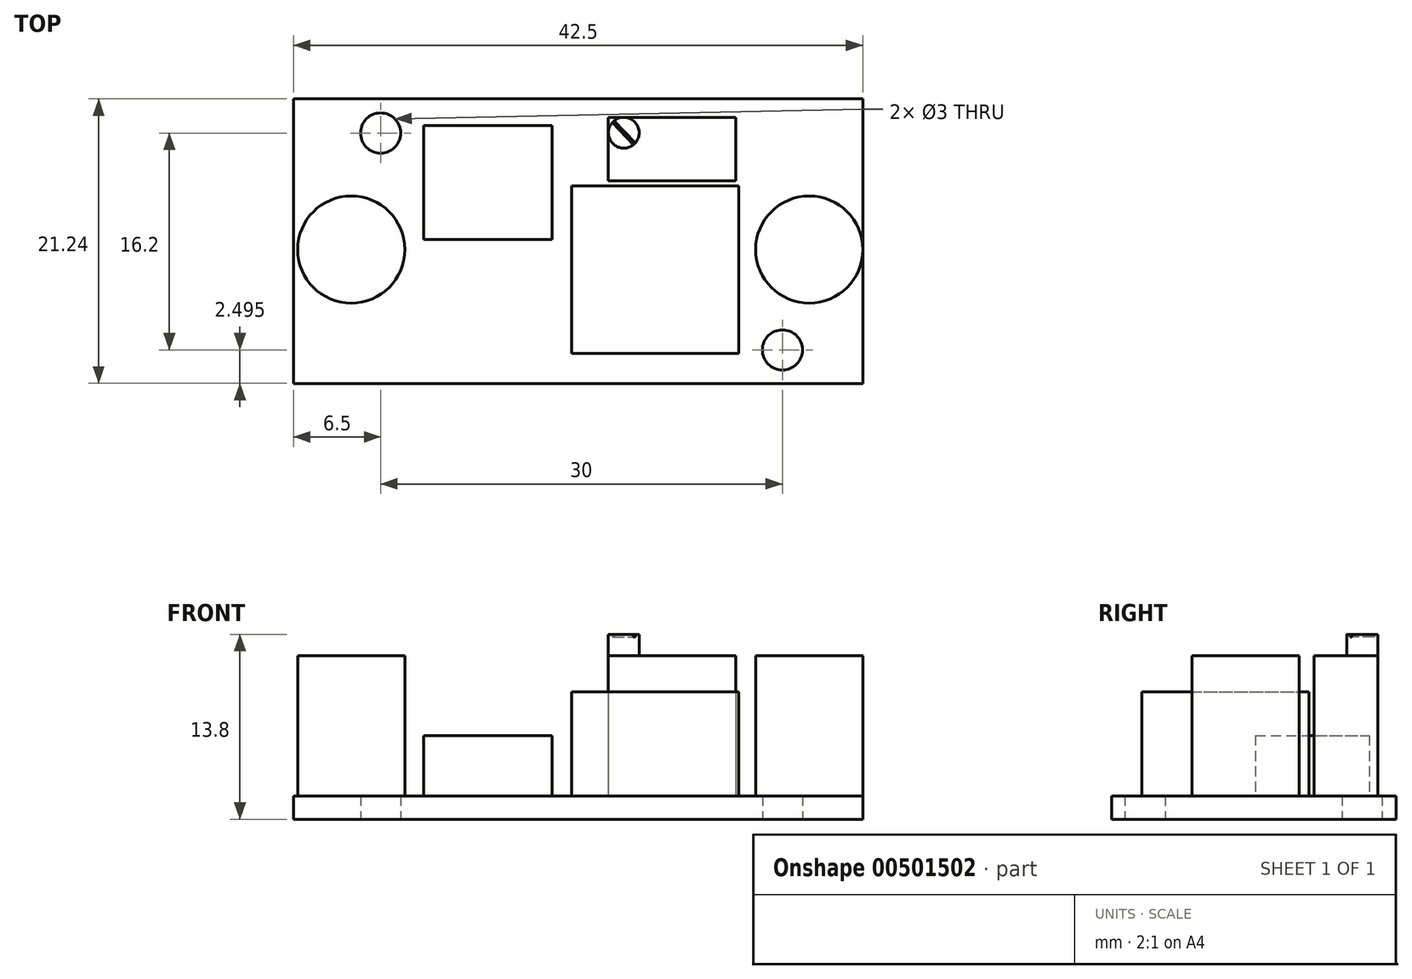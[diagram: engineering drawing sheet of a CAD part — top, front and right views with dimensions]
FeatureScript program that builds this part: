
annotation { "Feature Type Name" : "Feature", "Feature Type Description" : "" }
export const myFeature = defineFeature(function(context is Context, id is Id, definition is map)
    precondition{}
    {
        {
            var Q0;
            Q0=qCreatedBy(makeId("Top.planeOp"),FACE);
            var sketch = newSketch(context, id + "F0", { "sketchPlane" : qUnion([Q0])});
            skLineSegment(sketch, "E0.bottom", {"start": v(-21.25, -10.63) * mm, "end": v(21.25, -10.63) * mm});
            skLineSegment(sketch, "E0.top", {"start": v(-21.25, 10.62) * mm, "end": v(21.25, 10.62) * mm});
            skLineSegment(sketch, "E0.left", {"start": v(-21.25, -10.63) * mm, "end": v(-21.25, 10.62) * mm});
            skLineSegment(sketch, "E0.right", {"start": v(21.25, -10.62) * mm, "end": v(21.25, 10.62) * mm});
            skPoint(sketch, "E0.middle", {"position": v(0, 0) * mm});
            skLineSegment(sketch, "E1.0", {"start": v(-16.95, -10.63) * mm, "end": v(-16.95, 10.62) * mm, "construction": true});
            skLineSegment(sketch, "E2.0", {"start": v(-14.75, -10.63) * mm, "end": v(-14.75, 10.62) * mm, "construction": true});
            skLineSegment(sketch, "E3.0", {"start": v(-6.75, -12.63) * mm, "end": v(-6.75, 8.62) * mm, "construction": true});
            skLineSegment(sketch, "E4.0", {"start": v(5.75, -8.93) * mm, "end": v(5.75, 12.32) * mm, "construction": true});
            skLineSegment(sketch, "E5.0", {"start": v(7, -12.63) * mm, "end": v(7, 8.62) * mm, "construction": true});
            skLineSegment(sketch, "E6.0", {"start": v(15.25, -10.63) * mm, "end": v(15.25, 10.62) * mm, "construction": true});
            skLineSegment(sketch, "E7.0", {"start": v(17.25, -10.63) * mm, "end": v(17.25, 10.62) * mm, "construction": true});
            skLineSegment(sketch, "E8.0", {"start": v(-21.25, 8.07) * mm, "end": v(21.25, 8.07) * mm, "construction": true});
            skLineSegment(sketch, "E9.0", {"start": v(-21.25, -0.63) * mm, "end": v(21.25, -0.63) * mm, "construction": true});
            skLineSegment(sketch, "E10.0", {"start": v(-21.25, -2.13) * mm, "end": v(21.25, -2.13) * mm, "construction": true});
            skLineSegment(sketch, "E11.0", {"start": v(-21.25, 4.37) * mm, "end": v(21.25, 4.37) * mm, "construction": true});
            skCircle(sketch, "E12", {"center": v(-14.75, 8.07) * mm, "radius": 1.5 * mm});
            skLineSegment(sketch, "E13.bottom", {"start": v(-1.95, 0.12) * mm, "end": v(-11.55, 0.12) * mm});
            skLineSegment(sketch, "E13.top", {"start": v(-1.95, 8.62) * mm, "end": v(-11.55, 8.62) * mm});
            skLineSegment(sketch, "E13.left", {"start": v(-1.95, 0.12) * mm, "end": v(-1.95, 8.62) * mm});
            skLineSegment(sketch, "E13.right", {"start": v(-11.55, 0.12) * mm, "end": v(-11.55, 8.62) * mm});
            skPoint(sketch, "E13.middle", {"position": v(-6.75, 4.37) * mm});
            skPoint(sketch, "E14.middle", {"position": v(5.75, -0.63) * mm});
            skPoint(sketch, "E15.middle", {"position": v(7, 4.37) * mm});
            skLineSegment(sketch, "E16.0", {"start": v(-21.25, 6.87) * mm, "end": v(21.25, 6.87) * mm, "construction": true});
            skLineSegment(sketch, "E17.bottom", {"start": v(2.25, 4.5) * mm, "end": v(11.75, 4.5) * mm});
            skLineSegment(sketch, "E17.top", {"start": v(2.25, 9.25) * mm, "end": v(11.75, 9.25) * mm});
            skLineSegment(sketch, "E17.left", {"start": v(2.25, 4.5) * mm, "end": v(2.25, 9.25) * mm});
            skLineSegment(sketch, "E17.right", {"start": v(11.75, 4.5) * mm, "end": v(11.75, 9.25) * mm});
            skLineSegment(sketch, "E18.0", {"start": v(-21.25, -8.13) * mm, "end": v(21.25, -8.13) * mm, "construction": true});
            skCircle(sketch, "E19", {"center": v(15.25, -8.13) * mm, "radius": 1.5 * mm});
            skCircle(sketch, "E20", {"center": v(-16.95, -0.63) * mm, "radius": 4 * mm});
            skCircle(sketch, "E21", {"center": v(17.25, -0.63) * mm, "radius": 4 * mm});
            skLineSegment(sketch, "E22.bottom", {"start": v(12, -8.38) * mm, "end": v(-0.5, -8.38) * mm});
            skLineSegment(sketch, "E22.top", {"start": v(12, 4.12) * mm, "end": v(-0.5, 4.12) * mm});
            skLineSegment(sketch, "E22.left", {"start": v(12, -8.38) * mm, "end": v(12, 4.12) * mm});
            skLineSegment(sketch, "E22.right", {"start": v(-0.5, -8.38) * mm, "end": v(-0.5, 4.12) * mm});
            skPoint(sketch, "E22.middle", {"position": v(5.75, -2.13) * mm});
            skSolve(sketch);
        }
        {
            var Q0;
            Q0=makeQuery(id+"F0.imprint","IMPRINT",FACE,{"disambiguationData":[TD([[makeQuery(id+"F0.imprint","IMPRINT",EDGE,{"derivedFrom":sQuery(id+"F0.wireOp",EDGE,"E14.bottom")}),-1.0]])]});
            var Q1;
            {var subQ4=sQuery(id+"F0.wireOp",EDGE,"E0.bottom");Q1=makeQuery(id+"F0.imprint","IMPRINT",FACE,{"disambiguationData":[TD([[makeQuery(id+"F0.imprint","IMPRINT",EDGE,{"derivedFrom":subQ4}),1.0]])]});}
            var Q2;
            Q2=makeQuery(id+"F0.imprint","IMPRINT",FACE,{"disambiguationData":[TD([[makeQuery(id+"F0.imprint","IMPRINT",EDGE,{"derivedFrom":sQuery(id+"F0.wireOp",EDGE,"E17.bottom")}),1.0]])]});
            var Q3;
            Q3=makeQuery(id+"F0.imprint","IMPRINT",FACE,{"disambiguationData":[TD([[makeQuery(id+"F0.imprint","IMPRINT",EDGE,{"derivedFrom":sQuery(id+"F0.wireOp",EDGE,"E13.bottom")}),-1.0]])]});
            var Q4;
            Q4=makeQuery(id+"F0.imprint","IMPRINT",FACE,{"disambiguationData":[TD([[makeQuery(id+"F0.imprint","IMPRINT",EDGE,{"derivedFrom":sQuery(id+"F0.wireOp",EDGE,"E21")}),1.0]])]});
            var Q5;
            Q5=makeQuery(id+"F0.imprint","IMPRINT",FACE,{"disambiguationData":[TD([[makeQuery(id+"F0.imprint","IMPRINT",EDGE,{"derivedFrom":sQuery(id+"F0.wireOp",EDGE,"E20")}),1.0]])]});
            extrude(context, id + "F1", {"entities" : qUnion([Q0, Q1, Q2, Q3, Q4, Q5]), "depth" : 1.75 * mm});
        }
        {
            var Q0;
            Q0=makeQuery(id+"F0.imprint","IMPRINT",FACE,{"disambiguationData":[TD([[makeQuery(id+"F0.imprint","IMPRINT",EDGE,{"derivedFrom":sQuery(id+"F0.wireOp",EDGE,"E21")}),1.0]])]});
            var Q1;
            Q1=makeQuery(id+"F0.imprint","IMPRINT",FACE,{"disambiguationData":[TD([[makeQuery(id+"F0.imprint","IMPRINT",EDGE,{"derivedFrom":sQuery(id+"F0.wireOp",EDGE,"E17.bottom")}),1.0]])]});
            var Q2;
            Q2=makeQuery(id+"F0.imprint","IMPRINT",FACE,{"disambiguationData":[TD([[makeQuery(id+"F0.imprint","IMPRINT",EDGE,{"derivedFrom":sQuery(id+"F0.wireOp",EDGE,"E20")}),1.0]])]});
            extrude(context, id + "F2", {"entities" : qUnion([Q0, Q1, Q2]), "operationType" : NewBodyOperationType.ADD, "depth" : 12.2 * mm});
        }
        {
            var Q0;
            Q0=makeQuery(id+"F0.imprint","IMPRINT",FACE,{"disambiguationData":[TD([[makeQuery(id+"F0.imprint","IMPRINT",EDGE,{"derivedFrom":sQuery(id+"F0.wireOp",EDGE,"E13.bottom")}),-1.0]])]});
            extrude(context, id + "F3", {"entities" : qUnion([Q0]), "operationType" : NewBodyOperationType.ADD, "depth" : 6.25 * mm});
        }
        {
            var Q0;
            Q0=makeQuery(id+"F0.imprint","IMPRINT",FACE,{"disambiguationData":[TD([[makeQuery(id+"F0.imprint","IMPRINT",EDGE,{"derivedFrom":sQuery(id+"F0.wireOp",EDGE,"E22.bottom")}),-1.0]])]});
            extrude(context, id + "F4", {"entities" : qUnion([Q0]), "operationType" : NewBodyOperationType.ADD, "depth" : 9.5 * mm});
        }
        {
            var Q0;
            Q0=makeQuery(id+"F2.opExtrude","CAP_FACE",FACE,{"disambiguationData":[OSD([sQuery(id+"F0.wireOp",EDGE,"E17.bottom"),sQuery(id+"F0.wireOp",EDGE,"E17.top"),sQuery(id+"F0.wireOp",EDGE,"E17.left"),sQuery(id+"F0.wireOp",EDGE,"E17.right")])],"isStart":false});
            var sketch = newSketch(context, id + "F5", { "sketchPlane" : qUnion([Q0])});
            skCircle(sketch, "E23", {"center": v(3.4, 8.1) * mm, "radius": 1.15 * mm});
            skLineSegment(sketch, "E24", {"start": v(2.55, 8.86) * mm, "end": v(4.12, 7.2) * mm});
            skLineSegment(sketch, "E25", {"start": v(2.7, 9) * mm, "end": v(4.26, 7.33) * mm});
            skSolve(sketch);
        }
        {
            var Q0;
            {var subQ0=sQuery(id+"F5.wireOp",EDGE,"E24");Q0=makeQuery(id+"F5.imprint","IMPRINT",FACE,{"disambiguationData":[TD([[makeQuery(id+"F5.imprint","IMPRINT",EDGE,{"derivedFrom":subQ0}),-1.0]])]});}
            var Q1;
            {var subQ0=sQuery(id+"F5.wireOp",EDGE,"E25");Q1=makeQuery(id+"F5.imprint","IMPRINT",FACE,{"disambiguationData":[TD([[makeQuery(id+"F5.imprint","IMPRINT",EDGE,{"derivedFrom":subQ0}),1.0]])]});}
            extrude(context, id + "F6", {"entities" : qUnion([Q0, Q1]), "operationType" : NewBodyOperationType.ADD, "depth" : 1.6 * mm, "offsetDistance" : 25 * mm});
        }
        {
            var Q0;
            {var subQ0=sQuery(id+"F5.wireOp",EDGE,"E24");Q0=makeQuery(id+"F5.imprint","IMPRINT",FACE,{"disambiguationData":[TD([[makeQuery(id+"F5.imprint","IMPRINT",EDGE,{"derivedFrom":subQ0}),1.0]])]});}
            extrude(context, id + "F7", {"entities" : qUnion([Q0]), "operationType" : NewBodyOperationType.ADD, "depth" : 1.4 * mm, "offsetDistance" : 25 * mm});
        }
    });
